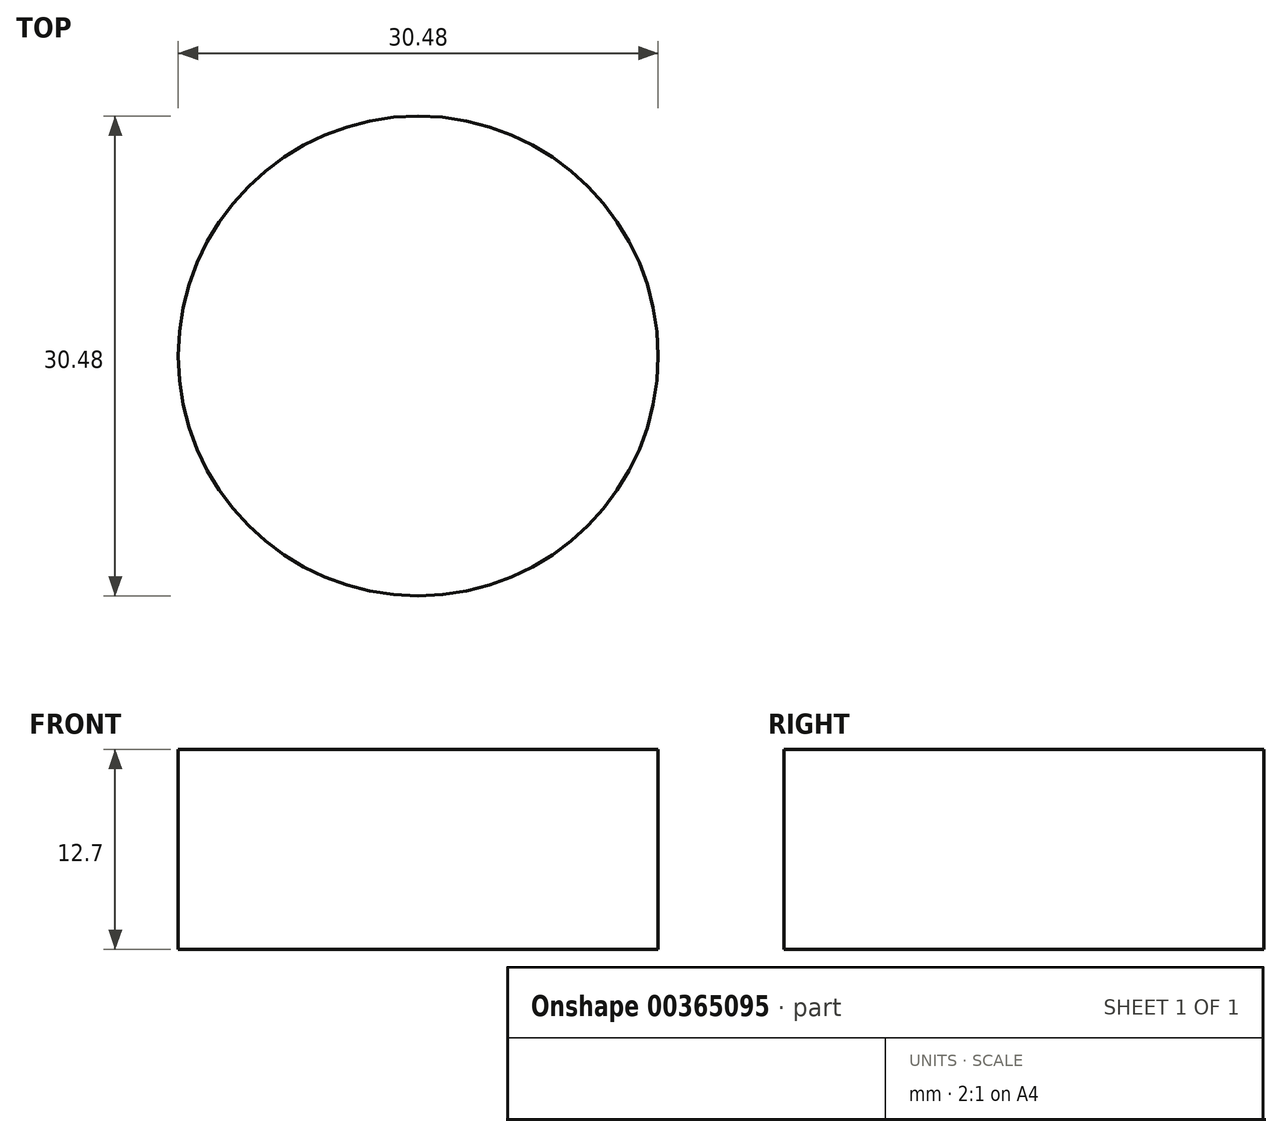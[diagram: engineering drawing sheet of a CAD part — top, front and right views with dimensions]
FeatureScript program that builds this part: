
annotation { "Feature Type Name" : "Feature", "Feature Type Description" : "" }
export const myFeature = defineFeature(function(context is Context, id is Id, definition is map)
    precondition{}
    {
        {
            var Q0;
            Q0=qCreatedBy(makeId("Top.planeOp"),FACE);
            var sketch = newSketch(context, id + "F0", { "sketchPlane" : qUnion([Q0])});
            skCircle(sketch, "E0", {"center": v(0, 0) * mm, "radius": 15.24 * mm});
            skPoint(sketch, "E1", {"position": v(15.24, 0) * mm});
            skPoint(sketch, "E2", {"position": v(-15.24, 0) * mm});
            skSolve(sketch);
        }
        {
            var Q0;
            Q0=makeQuery(id+"F0.imprint","IMPRINT",FACE,{"disambiguationData":[TD([[makeQuery(id+"F0.imprint","IMPRINT",EDGE,{"derivedFrom":sQuery(id+"F0.wireOp",EDGE,"E0")}),1.0]])]});
            extrude(context, id + "F1", {"entities" : qUnion([Q0]), "depth" : 12.7 * mm});
        }
    });
